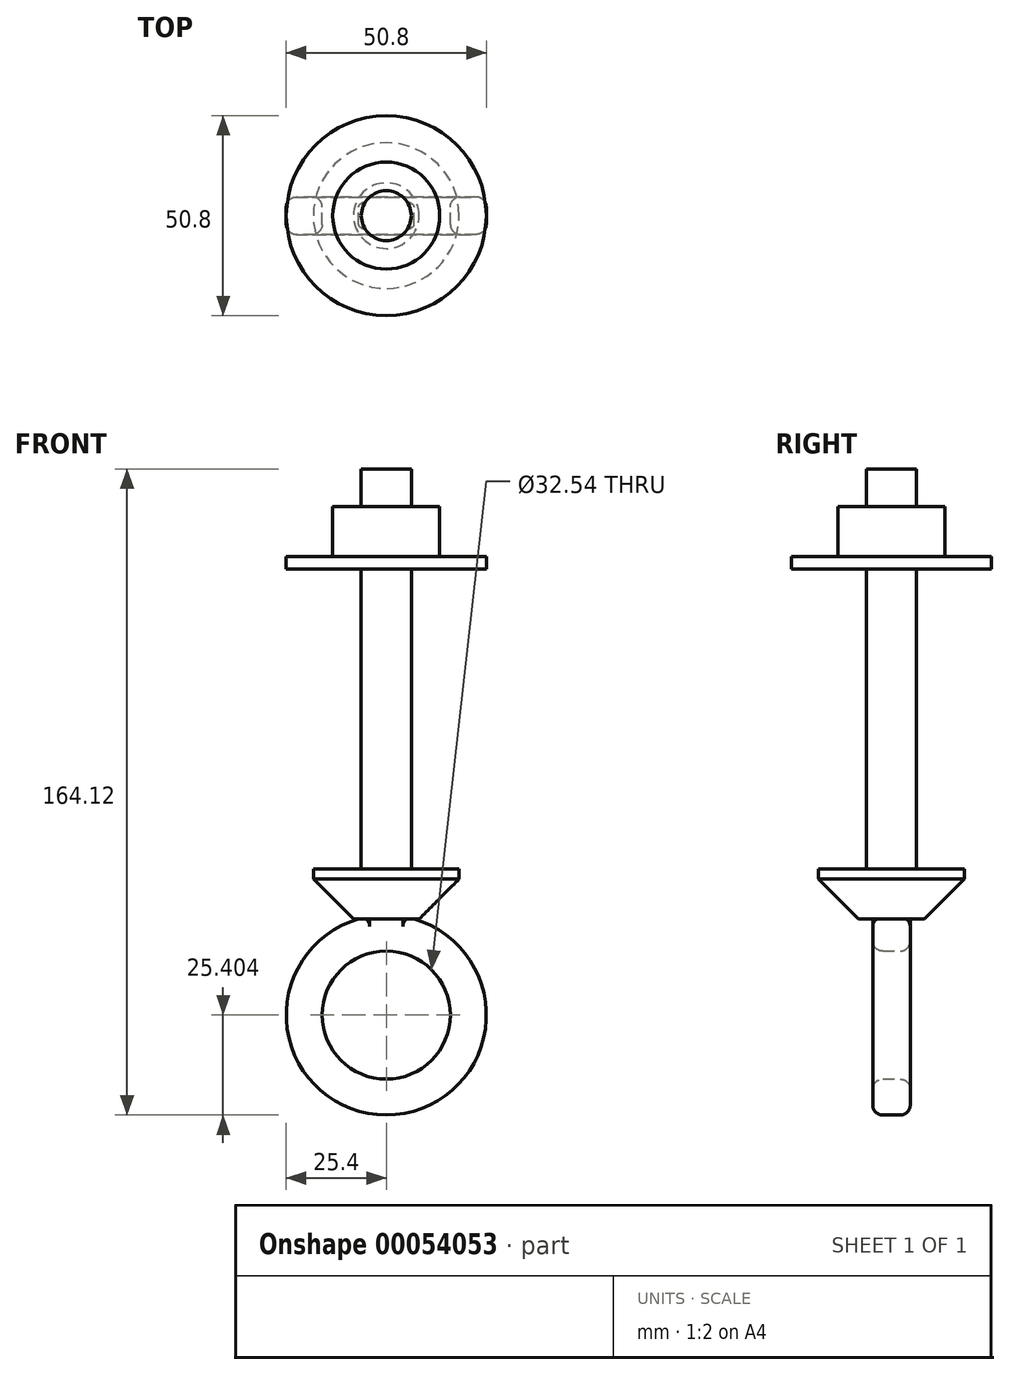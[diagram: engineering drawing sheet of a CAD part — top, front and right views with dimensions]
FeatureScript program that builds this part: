
annotation { "Feature Type Name" : "Feature", "Feature Type Description" : "" }
export const myFeature = defineFeature(function(context is Context, id is Id, definition is map)
    precondition{}
    {
        {
            var Q0;
            Q0=qCreatedBy(makeId("Top.planeOp"),FACE);
            var sketch = newSketch(context, id + "F0", { "sketchPlane" : qUnion([Q0])});
            skCircle(sketch, "E0", {"center": v(0, 0) * mm, "radius": 6.35 * mm});
            skSolve(sketch);
        }
        {
            var Q0;
            Q0=makeQuery(id+"F0.imprint","IMPRINT",FACE,{"disambiguationData":[TD([[makeQuery(id+"F0.imprint","IMPRINT",EDGE,{"derivedFrom":sQuery(id+"F0.wireOp",EDGE,"E0")}),1.0]])]});
            extrude(context, id + "F1", {"entities" : qUnion([Q0]), "depth" : 114.3 * mm});
        }
        {
            var Q0;
            Q0=qCreatedBy(makeId("Front.planeOp"),FACE);
            var sketch = newSketch(context, id + "F2", { "sketchPlane" : qUnion([Q0])});
            skCircle(sketch, "E1", {"center": v(0, -24.42) * mm, "radius": 25.4 * mm});
            skCircle(sketch, "E2", {"center": v(0, -24.42) * mm, "radius": 16.27 * mm});
            skSolve(sketch);
        }
        {
            var Q0;
            Q0=makeQuery(id+"F2.imprint","IMPRINT",FACE,{"disambiguationData":[TD([[makeQuery(id+"F2.imprint","IMPRINT",EDGE,{"derivedFrom":sQuery(id+"F2.wireOp",EDGE,"E1")}),1.0]])]});
            extrude(context, id + "F3", {"entities" : qUnion([Q0]), "operationType" : NewBodyOperationType.ADD, "depth" : 9.52 * mm, "symmetric" : true});
        }
        {
            var Q0;
            Q0=makeQuery(id+"F3.opExtrude","SWEPT_FACE",FACE,{"disambiguationData":[OSD([sQuery(id+"F2.wireOp",EDGE,"E2")])]});
            var Q1;
            Q1=makeQuery(id+"F3.opExtrude","CAP_EDGE",EDGE,{"disambiguationData":[OSD([sQuery(id+"F2.wireOp",EDGE,"E1")])],"isStart":true});
            var Q2;
            Q2=makeQuery(id+"F3.opExtrude","CAP_EDGE",EDGE,{"disambiguationData":[OSD([sQuery(id+"F2.wireOp",EDGE,"E1")])],"isStart":false});
            var Q3;
            Q3=makeQuery(id+"F3.opExtrude","CAP_EDGE",EDGE,{"disambiguationData":[OSD([sQuery(id+"F2.wireOp",EDGE,"E2")])],"isStart":false});
            fillet(context, id + "F4", {"entities" : qUnion([Q0, Q1, Q2, Q3]), "radius" : 2.54 * mm, "tangentPropagation" : true, "allowEdgeOverflow" : false});
        }
        {
            var Q0;
            Q0=qCreatedBy(makeId("Top.planeOp"),FACE);
            cPlane(context, id + "F5", {"entities" : qUnion([Q0]), "cplaneType" : CPlaneType.OFFSET, "offset" : 88.9 * mm, "width" : 152.4 * mm, "height" : 152.4 * mm});
        }
        {
            var Q0;
            Q0=qCreatedBy(id+"F5.planeOp",FACE);
            var sketch = newSketch(context, id + "F6", { "sketchPlane" : qUnion([Q0])});
            skCircle(sketch, "E3", {"center": v(0, 0) * mm, "radius": 25.4 * mm});
            skSolve(sketch);
        }
        {
            var Q0;
            Q0=makeQuery(id+"F6.imprint","IMPRINT",FACE,{"disambiguationData":[TD([[makeQuery(id+"F6.imprint","IMPRINT",EDGE,{"derivedFrom":sQuery(id+"F6.wireOp",EDGE,"E3")}),1.0]])]});
            extrude(context, id + "F7", {"entities" : qUnion([Q0]), "operationType" : NewBodyOperationType.ADD, "depth" : 3.17 * mm});
        }
        {
            var Q0;
            Q0=makeQuery(id+"F7.opExtrude","CAP_FACE",FACE,{"disambiguationData":[OSD([sQuery(id+"F6.wireOp",EDGE,"E3")])],"isStart":false});
            var sketch = newSketch(context, id + "F8", { "sketchPlane" : qUnion([Q0])});
            skCircle(sketch, "E4", {"center": v(0, 0) * mm, "radius": 13.6 * mm});
            skSolve(sketch);
        }
        {
            var Q0;
            Q0=makeQuery(id+"F8.imprint","IMPRINT",FACE,{"disambiguationData":[TD([[makeQuery(id+"F8.imprint","IMPRINT",EDGE,{"derivedFrom":sQuery(id+"F8.wireOp",EDGE,"E4")}),1.0]])]});
            extrude(context, id + "F9", {"entities" : qUnion([Q0]), "operationType" : NewBodyOperationType.ADD, "depth" : 12.7 * mm});
        }
        {
            var Q0;
            Q0=qCreatedBy(makeId("Top.planeOp"),FACE);
            var sketch = newSketch(context, id + "F10", { "sketchPlane" : qUnion([Q0])});
            skCircle(sketch, "E5", {"center": v(0, 0) * mm, "radius": 18.51 * mm});
            skSolve(sketch);
        }
        {
            var Q0;
            Q0=makeQuery(id+"F10.imprint","IMPRINT",FACE,{"disambiguationData":[TD([[makeQuery(id+"F10.imprint","IMPRINT",EDGE,{"derivedFrom":sQuery(id+"F10.wireOp",EDGE,"E5")}),1.0]])]});
            extrude(context, id + "F11", {"entities" : qUnion([Q0]), "operationType" : NewBodyOperationType.ADD, "depth" : 12.7 * mm});
        }
        {
            var Q0;
            Q0=makeQuery(id+"F11.opExtrude","CAP_EDGE",EDGE,{"disambiguationData":[OSD([sQuery(id+"F10.wireOp",EDGE,"E5")])],"isStart":true});
            chamfer(context, id + "F12", {"entities" : qUnion([Q0]), "width" : 10.16 * mm, "tangentPropagation" : true});
        }
    });
